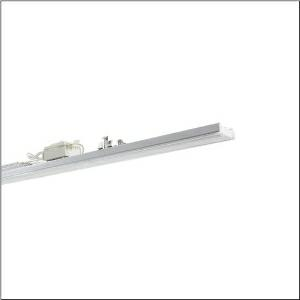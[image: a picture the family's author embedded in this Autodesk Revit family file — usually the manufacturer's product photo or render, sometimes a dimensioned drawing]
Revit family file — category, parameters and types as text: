
# Revit family: licross_11_recessed_mo_51tl12dv4fxg3s4
name_source: partatom
category: Lighting Fixtures
units: mm (PartAtom-declared; Revit-internal decimal feet)

## family parameters
Cut with Voids When Loaded = No
Host = Face
Light Source = No
Part Type = Normal
Room Calculation Point = No
Round Connector Dimension = Use Diameter
Shared = No

## types (1)
- --- (1 x LED, 1010 lm, 5.5 W, 4000K)
    Apparent Load = 6 VA
    CIE Flux Codes = 67 92 99 100 100
    Color Rendering = 80
    Color Temperature = 4000K
    Default Elevation = 1800 mm
    Description = Licross 11 Recessed MO, luminaire insert, of sheet steel, coil coated, white, length: 2.250mm, width: 66mm, height: 67mm, LED rated luminous flux: 15.360lm, light colour: 840, SDCM (Standard Deviation of Colour Matching)MacAdam ≤ 2 SDCM (initial), control gear: DALI 2, with plug, 6-pole, with phase selection, for trunking rail, 9 or 11-core, mains connection: 220..240V, AC, 50/60Hz, rated input power: 88W, for trunking rail, 9-/11-core, internal wiring halogen-free, for emergency light function, converter,control gear: single battery element, battery: LiFePO4, 9Ah, primary optical cover: cover, of PMMA, light emission: direct distribution, primary light characteristic: symmetric, protection rating (complete): IP40, insulation class (complete): insulation class I (protective earthing), certification: CE, UKCA, protection symbol: D if used in an environment without relevant dust loads with corresponding accessories, impact resistance: IK06, permissible ambient temperature for indoor applications: +5..+35°C, standard: EN 60598-2-22, LABS conformity tested according to VDMA 24364:2018-05, reducing of maximum allowable ambient temperature of 5°C with ceiling mounting, corresponds to IFS (International Featured Standards) requirements for safety and quality in the food industry, The light source and the operating device comply with the requirements of the Ecodesign Regulation (EU) 2019/2020 and are replaceable in accordance with this regulation, packaging unit: 1 piece
    Height = 58 mm
    Lamp = 1 x LED
    Lamp Light Flux = 1010 lm
    Lamp Power = 5.5 W
    Lamp count = 1
    Length = 2250 mm
    Luminous efficacy = 184 lm/W
    Manufacturer = Siteco
    ModVariant = No
    Model = 51TL12DV4FXG3S4
    Mounting Place = Ceiling
    Mounting Type = Pendant
    Number of Poles = 1
    OnlyDefault = Yes
    Power Factor = 1
    Product Name = Licross 11 Recessed MO
    Product group = luminaire insert | ceiling pendant
    ProductGroupID = 901
    Protection Class = Protection class I
    Protection Degree = IP 40
    RLX_Detail_Level = 1
    RLX_Emergency_Light_Flux = 0 lm
    RLX_Emergency_Type = 0
    RLX_Emergency_Type_DB = No
    RlxData = <blob elided: 30009 chars, md5=9bfaac99>
    Socket = socket
    Standby Power = 0 W
    System Light Flux = 1010 lm
    System Power = 6 W
    Type Comments = : emergency light operation: 3 h
    Type Image = l_1296930.jpg
    URL = http://relux.com
    VarID = @adj_090017
    Voltage = 0 V
    Weight = 0.00 kg
    Width = 66 mm

## geometry (parser evidence)
native form markers: Blend x4, Sweep x9
no freeform markers — native parametric forms only
